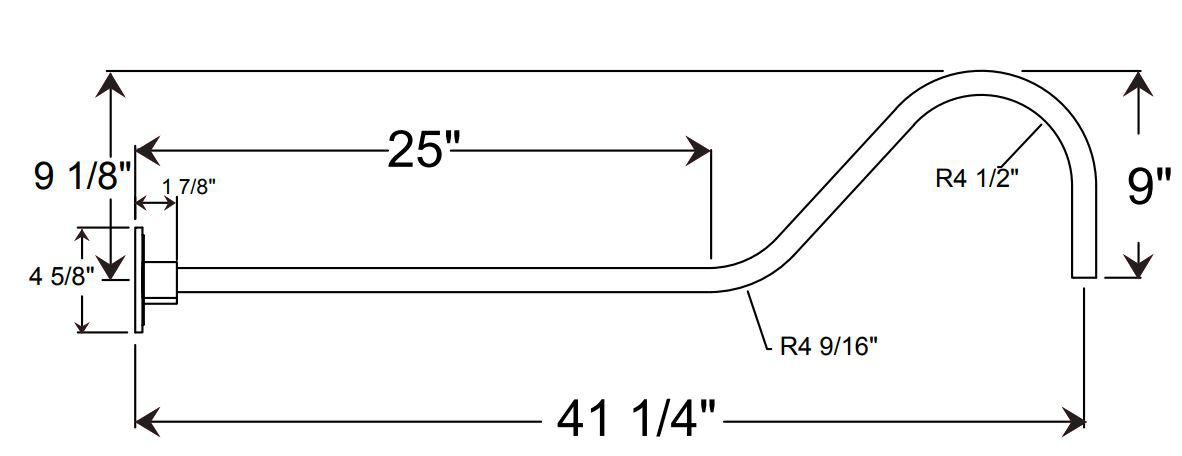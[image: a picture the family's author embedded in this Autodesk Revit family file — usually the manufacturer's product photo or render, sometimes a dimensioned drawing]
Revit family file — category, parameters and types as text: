
# Revit family: MILKCAN FT(8,10,12,18) LED
name_source: partatom
category: Lighting Fixtures
units: mm (PartAtom-declared; Revit-internal decimal feet)

## family parameters
Always vertical = Yes
Cut with Voids When Loaded = No
Light Source = Yes
OmniClass Number = 23.80.70.00
OmniClass Title = Lighting
Part Type = Normal
Room Calculation Point = No
Round Connector Dimension = Use Diameter
Shared = No
Work Plane-Based = No

## types (4) — shared parameters
Body Colour = Spun aluminium
Body Material = body
CRI = >90
Color Filter = 16777215
Construction Material = Heavy Duty spun aluminum.
Default Elevation = 0' - 0"
Description = 120-277 Voltage
Dimming = 1%
Dimming Lamp Color Temperature Shift = <None>
Efficiency = 65-125 lumens per watt
Lamp = LED
Life = L70 50,000 hours
Load Classification = Lighting
Manufacturer = ANP Lighting
Photometric Web File = generic.ies
Power Factor = 1
Tilt Angle = 90.00°
URL = https://www.anplighting.com
Voltage = 277 V
Warranty = 5 year limited warranty

## per-type parameters (varying)
| type | Apparent Load | Fixture Diameter | Fixture Height | MCFT08 | MCFT10 | MCFT12 | MCFT18 | Wattage Comments | Weight |
| MCFT08 | 9 VA | 0' - 8" | 0' - 5" | Yes | No | No | No | 9W | 1 lbs |
| MCFT10 | 10 VA | 0' - 10" | 0' - 5 1/2" | No | Yes | No | No | 10W | 1 lbs |
| MCFT12 | 16 VA | 1' - 0" | 0' - 7" | No | No | Yes | No | 16W | 1.5 lbs |
| MCFT18 | 24 VA | 1' - 6" | 0' - 8 1/2" | No | No | No | Yes | 24W | 1.5 lbs |

note: column(s) folded — value = type name in every type: Model

## geometry (parser evidence)
native form markers: Sweep x27
no freeform markers — native parametric forms only
